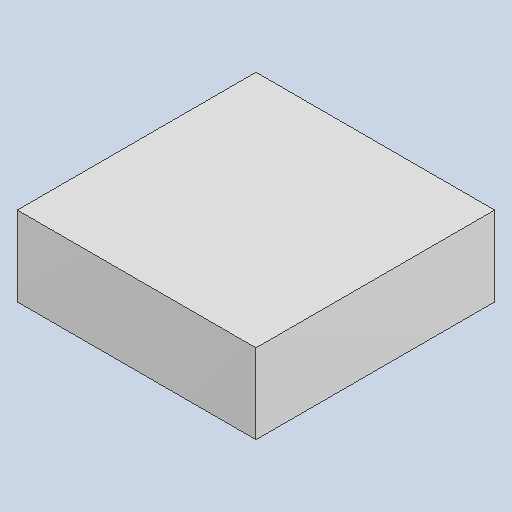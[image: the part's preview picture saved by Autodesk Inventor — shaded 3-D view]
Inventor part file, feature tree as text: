
AUTODESK INVENTOR PART (.ipt)
format: ipt  version: 2023.4 (Build 274418000, 418)  size: 79,872 bytes
history: native  units: mm
features: extrude x1
ambient origin geometry x8: Origin, YZ Plane, XZ Plane, XY Plane, X Axis, Y Axis, Z Axis, Center Point
bodies: Solid1 (feature_tree)
feature tree (1):
  extrude  "Extruded_48"  [1 undecoded]
note: 1 required parameter value undecoded (feature->parameter linkage not recoverable at this tier; creation-order binding heuristic only, values carry confidence <= 0.55)
